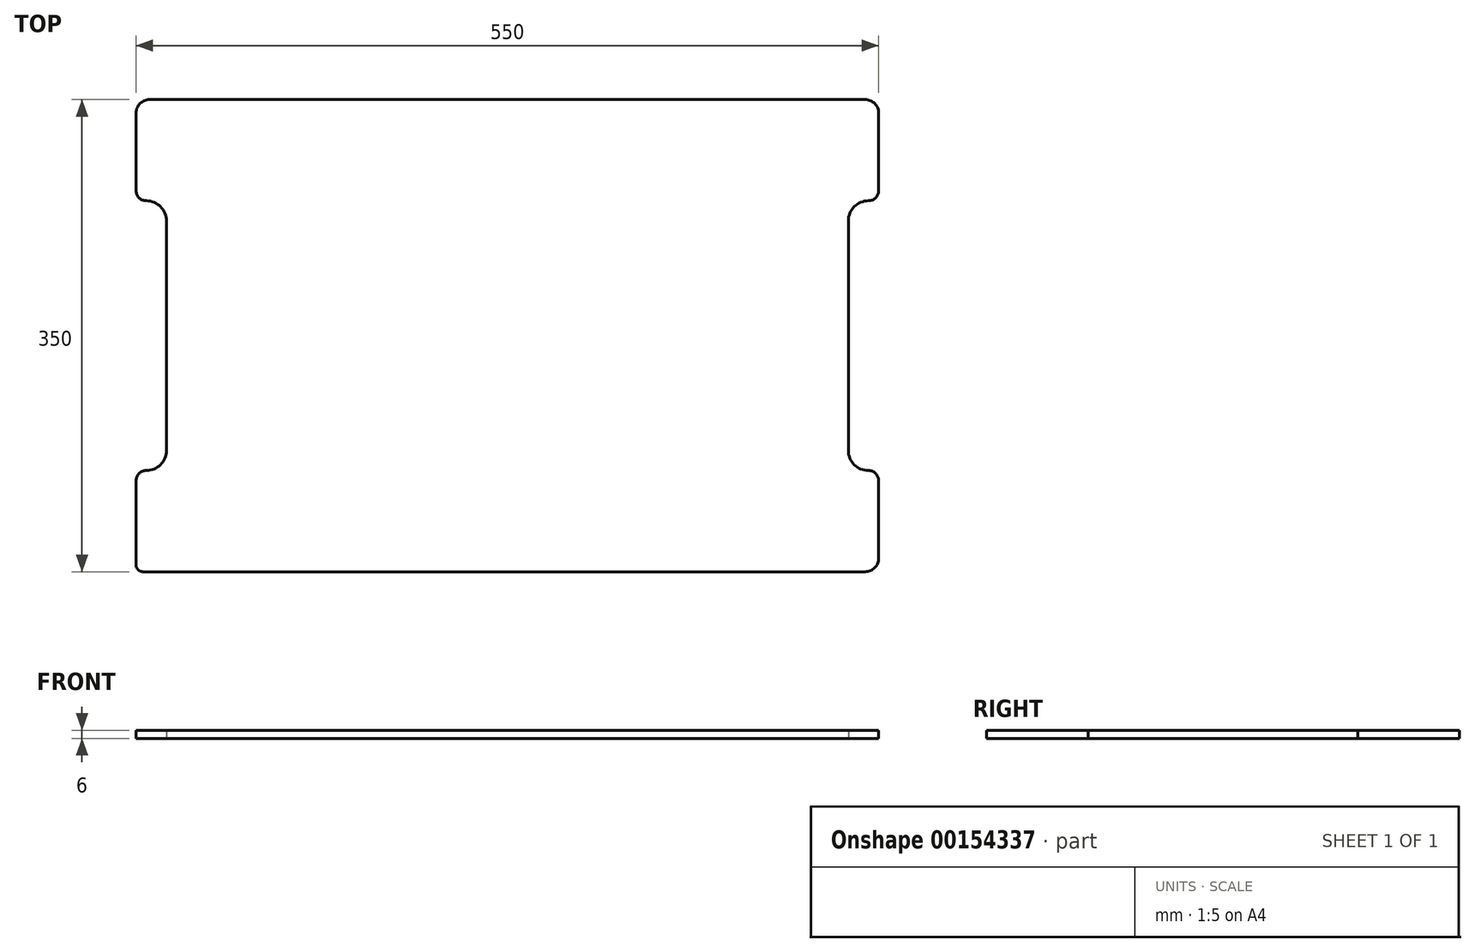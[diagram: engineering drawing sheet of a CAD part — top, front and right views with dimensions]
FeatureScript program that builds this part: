
annotation { "Feature Type Name" : "Feature", "Feature Type Description" : "" }
export const myFeature = defineFeature(function(context is Context, id is Id, definition is map)
    precondition{}
    {
        {
            var Q0;
            Q0=qCreatedBy(makeId("Top.planeOp"),FACE);
            var sketch = newSketch(context, id + "F0", { "sketchPlane" : qUnion([Q0])});
            skLineSegment(sketch, "E0.bottom", {"start": v(265, 175) * mm, "end": v(-265, 175) * mm});
            skLineSegment(sketch, "E0.top", {"start": v(265, -175) * mm, "end": v(-270, -175) * mm});
            skLineSegment(sketch, "E0.left", {"start": v(275, 175) * mm, "end": v(275, -175) * mm, "construction": true});
            skLineSegment(sketch, "E0.right", {"start": v(-275, 175) * mm, "end": v(-275, -175) * mm, "construction": true});
            skPoint(sketch, "E0.middle", {"position": v(0, 0) * mm});
            skLineSegment(sketch, "E1.bottom", {"start": v(252.5, 165) * mm, "end": v(-252.5, 165) * mm, "construction": true});
            skLineSegment(sketch, "E1.top", {"start": v(252.5, -165) * mm, "end": v(-252.5, -165) * mm, "construction": true});
            skLineSegment(sketch, "E1.left", {"start": v(252.5, 165) * mm, "end": v(252.5, -165) * mm, "construction": true});
            skLineSegment(sketch, "E1.right", {"start": v(-252.5, 165) * mm, "end": v(-252.5, -165) * mm, "construction": true});
            skLineSegment(sketch, "E2", {"start": v(-275, 0) * mm, "end": v(-252.5, 0) * mm, "construction": true});
            skLineSegment(sketch, "E3", {"start": v(252.5, 0) * mm, "end": v(275, 0) * mm, "construction": true});
            skLineSegment(sketch, "E4", {"start": v(-275, 165) * mm, "end": v(-275, 107.5) * mm});
            skLineSegment(sketch, "E5", {"start": v(-275, -170) * mm, "end": v(-275, -107.5) * mm});
            skLineSegment(sketch, "E6", {"start": v(275, -165) * mm, "end": v(275, -107.5) * mm});
            skLineSegment(sketch, "E7", {"start": v(275, 165) * mm, "end": v(275, 107.5) * mm});
            skArc(sketch, "E8", {"start": v(-275, 107.5) * mm, "mid": v(-272.8, 102.2) * mm, "end": v(-267.5, 100) * mm});
            skArc(sketch, "E9", {"start": v(-252.5, 85) * mm, "mid": v(-256.9, 95.6) * mm, "end": v(-267.5, 100) * mm});
            skArc(sketch, "E10", {"start": v(-267.5, -100) * mm, "mid": v(-272.8, -102.2) * mm, "end": v(-275, -107.5) * mm});
            skArc(sketch, "E11", {"start": v(-267.5, -100) * mm, "mid": v(-256.9, -95.6) * mm, "end": v(-252.5, -85) * mm});
            skLineSegment(sketch, "E12", {"start": v(-252.5, 85) * mm, "end": v(-252.5, -85) * mm});
            skLineSegment(sketch, "E13", {"start": v(0, 175) * mm, "end": v(0, -175) * mm, "construction": true});
            skArc(sketch, "E14.MirrorCS", {"start": v(275, 107.5) * mm, "mid": v(272.8, 102.2) * mm, "end": v(267.5, 100) * mm});
            skArc(sketch, "E15.MirrorCS", {"start": v(252.5, 85) * mm, "mid": v(256.9, 95.6) * mm, "end": v(267.5, 100) * mm});
            skArc(sketch, "E16.MirrorCS", {"start": v(267.5, -100) * mm, "mid": v(256.9, -95.6) * mm, "end": v(252.5, -85) * mm});
            skArc(sketch, "E17.MirrorCS", {"start": v(267.5, -100) * mm, "mid": v(272.8, -102.2) * mm, "end": v(275, -107.5) * mm});
            skLineSegment(sketch, "E18.MirrorCS", {"start": v(252.5, 85) * mm, "end": v(252.5, -85) * mm});
            skLineSegment(sketch, "E19.MirrorCS", {"start": v(275, 0) * mm, "end": v(252.5, 0) * mm, "construction": true});
            skPoint(sketch, "E20.visualSharp", {"position": v(-275, 175) * mm});
            skArc(sketch, "E20.filletArc", {"start": v(-265, 175) * mm, "mid": v(-272.07, 172.07) * mm, "end": v(-275, 165) * mm});
            skPoint(sketch, "E21.visualSharp", {"position": v(-275, -175) * mm});
            skArc(sketch, "E21.filletArc", {"start": v(-275, -170) * mm, "mid": v(-273.54, -173.54) * mm, "end": v(-270, -175) * mm});
            skPoint(sketch, "E22.visualSharp", {"position": v(275, 175) * mm});
            skArc(sketch, "E22.filletArc", {"start": v(275, 165) * mm, "mid": v(272.07, 172.07) * mm, "end": v(265, 175) * mm});
            skPoint(sketch, "E23.visualSharp", {"position": v(275, -175) * mm});
            skArc(sketch, "E23.filletArc", {"start": v(265, -175) * mm, "mid": v(272.07, -172.07) * mm, "end": v(275, -165) * mm});
            skSolve(sketch);
        }
        {
            var Q0;
            Q0 = qSketchRegion(id + "F0", true);
            extrude(context, id + "F1", {"entities" : qUnion([Q0]), "depth" : 6 * mm});
        }
    });
